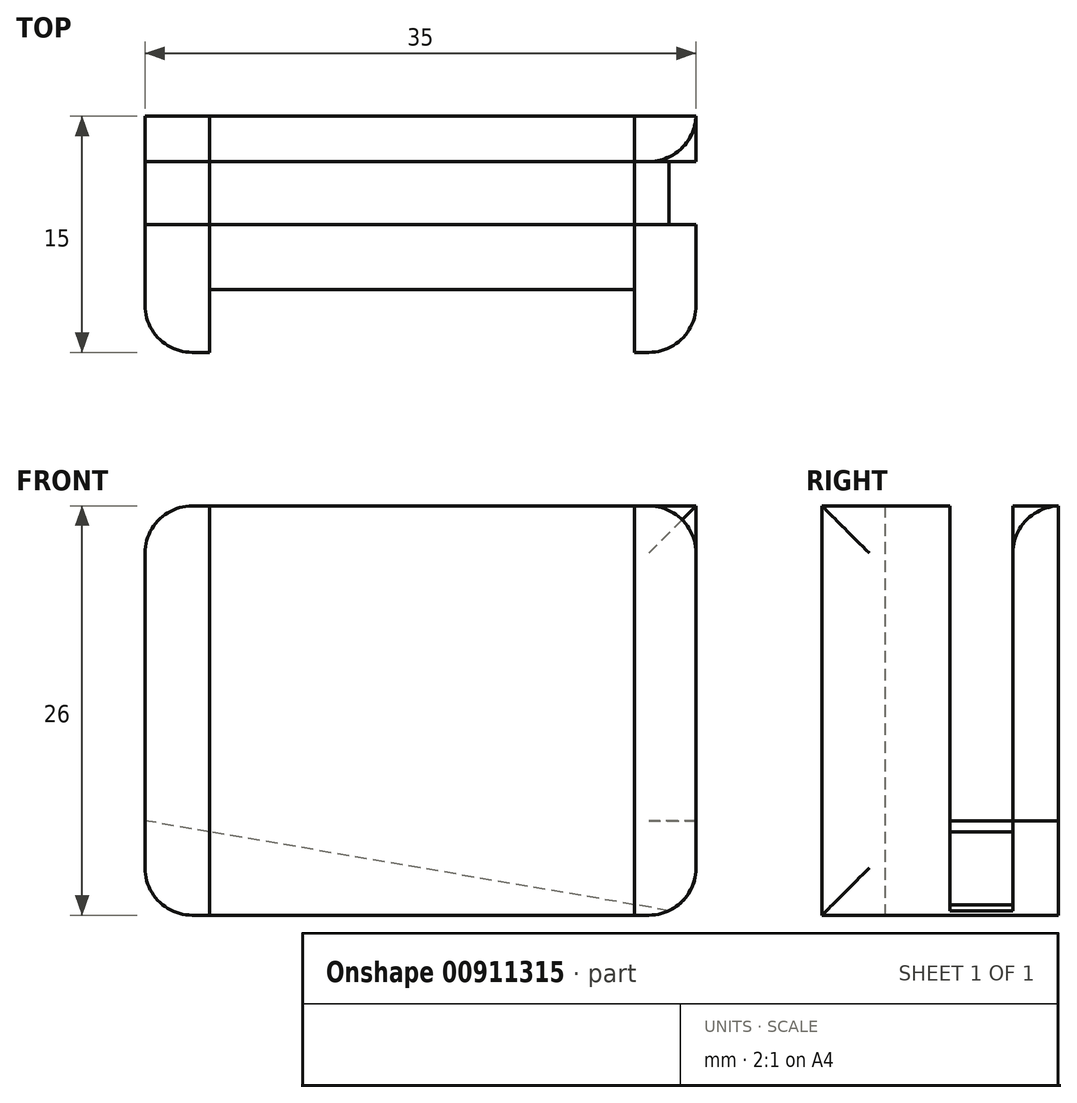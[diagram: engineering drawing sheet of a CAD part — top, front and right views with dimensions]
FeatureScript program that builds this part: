
annotation { "Feature Type Name" : "Feature", "Feature Type Description" : "" }
export const myFeature = defineFeature(function(context is Context, id is Id, definition is map)
    precondition{}
    {
        {
            var Q0;
            Q0=qCreatedBy(makeId("Front.planeOp"),FACE);
            var sketch = newSketch(context, id + "F0", { "sketchPlane" : qUnion([Q0])});
            skLineSegment(sketch, "E0.bottom", {"start": v(13, 13) * mm, "end": v(-14, 13) * mm});
            skLineSegment(sketch, "E0.top", {"start": v(14, -13) * mm, "end": v(-13, -13) * mm});
            skLineSegment(sketch, "E0.left", {"start": v(14, 13) * mm, "end": v(14, -13) * mm});
            skLineSegment(sketch, "E0.right", {"start": v(-13, 13) * mm, "end": v(-13, -13) * mm});
            skPoint(sketch, "E0.middle", {"position": v(0, 0) * mm});
            skLineSegment(sketch, "E1.bottom", {"start": v(17.91, 13) * mm, "end": v(-17.09, 13) * mm});
            skLineSegment(sketch, "E1.top", {"start": v(17.91, -13) * mm, "end": v(-17.09, -13) * mm});
            skLineSegment(sketch, "E1.left", {"start": v(17.91, 13) * mm, "end": v(17.91, -13) * mm});
            skLineSegment(sketch, "E1.right", {"start": v(-17.09, 13) * mm, "end": v(-17.09, -13) * mm});
            skSolve(sketch);
        }
        {
            var Q0;
            {var subQ0=sQuery(id+"F0.wireOp",EDGE,"E0.right");Q0=makeQuery(id+"F0.imprint","IMPRINT",FACE,{"disambiguationData":[TD([[makeQuery(id+"F0.imprint","IMPRINT",EDGE,{"derivedFrom":subQ0}),-1.0]])]});}
            var Q1;
            {var subQ0=sQuery(id+"F0.wireOp",EDGE,"E0.left");Q1=makeQuery(id+"F0.imprint","IMPRINT",FACE,{"disambiguationData":[TD([[makeQuery(id+"F0.imprint","IMPRINT",EDGE,{"derivedFrom":subQ0}),1.0]])]});}
            extrude(context, id + "F1", {"entities" : qUnion([Q0, Q1]), "depth" : 15 * mm, "offsetDistance" : 25 * mm});
        }
        {
            var Q0;
            {var subQ0=sQuery(id+"F0.wireOp",EDGE,"E0.left");Q0=makeQuery(id+"F0.imprint","IMPRINT",FACE,{"disambiguationData":[TD([[makeQuery(id+"F0.imprint","IMPRINT",EDGE,{"derivedFrom":subQ0}),-1.0]])]});}
            extrude(context, id + "F2", {"entities" : qUnion([Q0]), "depth" : 11 * mm, "offsetDistance" : 25 * mm});
        }
        {
            var Q0;
            Q0=makeQuery(id+"F2.opExtrude","SWEPT_FACE",FACE,{"disambiguationData":[OSD([sQuery(id+"F0.wireOp",EDGE,"E1.bottom")])]});
            var sketch = newSketch(context, id + "F3", { "sketchPlane" : qUnion([Q0])});
            skLineSegment(sketch, "E2.bottom", {"start": v(25.5, -2.88) * mm, "end": v(-24.5, -2.88) * mm});
            skLineSegment(sketch, "E2.top", {"start": v(25.5, -6.88) * mm, "end": v(-24.5, -6.88) * mm});
            skLineSegment(sketch, "E2.left", {"start": v(25.5, -2.88) * mm, "end": v(25.5, -6.88) * mm});
            skLineSegment(sketch, "E2.right", {"start": v(-24.5, -2.88) * mm, "end": v(-24.5, -6.88) * mm});
            skPoint(sketch, "E2.middle", {"position": v(0.5, -4.88) * mm});
            skPoint(sketch, "E2.middle.positionSnap0", {"position": v(0.5, -11) * mm});
            skPoint(sketch, "E2.centerSnap0", {"position": v(0.5, -11) * mm});
            skSolve(sketch);
        }
        {
            var Q0;
            Q0 = qSketchRegion(id + "F3", true);
            extrude(context, id + "F4", {"entities" : qUnion([Q0]), "operationType" : NewBodyOperationType.REMOVE, "oppositeDirection" : true, "depth" : 20 * mm, "offsetDistance" : 25 * mm});
        }
        {
            var Q0;
            Q0=makeQuery(id+"F1.opExtrude","SWEPT_EDGE",EDGE,{"disambiguationData":[OSD([sQuery(id+"F0.wireOp",EDGE,"E1.top"),sQuery(id+"F0.wireOp",EDGE,"E1.left")])]});
            cPoint(context, id + "F5", {"entities" : qUnion([Q0]), "parameter" : 0.5});
        }
        {
            var Q0;
            {var subQ0=sQuery(id+"F3.wireOp",EDGE,"E2.bottom");Q0=makeQuery(id+"F4.boolean.opBoolean","INTERSECT",VERTEX,{"derivedFrom":[makeQuery(id+"F1.opExtrude","SWEPT_FACE",FACE,{"disambiguationData":[OSD([sQuery(id+"F0.wireOp",EDGE,"E1.right")])]}),makeQuery(id+"F4.opExtrude","SWEPT_FACE",FACE,{"disambiguationData":[OSD([subQ0])]}),makeQuery(id+"F4.opExtrude","CAP_FACE",FACE,{"disambiguationData":[OSD([subQ0,sQuery(id+"F3.wireOp",EDGE,"E2.top"),sQuery(id+"F3.wireOp",EDGE,"E2.left"),sQuery(id+"F3.wireOp",EDGE,"E2.right")])],"isStart":false})]});}
            var Q1;
            {var subQ0=sQuery(id+"F3.wireOp",EDGE,"E2.top");Q1=makeQuery(id+"F4.boolean.opBoolean","INTERSECT",VERTEX,{"derivedFrom":[makeQuery(id+"F1.opExtrude","SWEPT_FACE",FACE,{"disambiguationData":[OSD([sQuery(id+"F0.wireOp",EDGE,"E1.right")])]}),makeQuery(id+"F4.opExtrude","CAP_FACE",FACE,{"disambiguationData":[OSD([sQuery(id+"F3.wireOp",EDGE,"E2.bottom"),subQ0,sQuery(id+"F3.wireOp",EDGE,"E2.left"),sQuery(id+"F3.wireOp",EDGE,"E2.right")])],"isStart":false}),makeQuery(id+"F4.opExtrude","SWEPT_FACE",FACE,{"disambiguationData":[OSD([subQ0])]})]});}
            var Q2;
            Q2 = qCreatedBy(id + "F5" ,VERTEX);
            cPlane(context, id + "F6", {"entities" : qUnion([Q0, Q1, Q2]), "cplaneType" : CPlaneType.THREE_POINT, "offset" : 25 * mm, "width" : 150 * mm, "height" : 150 * mm});
        }
        {
            var Q0;
            {var subQ0=sQuery(id+"F0.wireOp",EDGE,"E1.bottom");var subQ1=sQuery(id+"F3.wireOp",EDGE,"E2.top");Q0=makeQuery(id+"F4.boolean.opBoolean","COPY",EDGE,{"disambiguationData":[topologyDisambiguationEdgeConnected([makeQuery(id+"F1.opExtrude","SWEPT_FACE",FACE,{"disambiguationData":[OSD([subQ0]),TDD([makeQuery(id+"F0.imprint","IMPRINT",EDGE,{"disambiguationData":[TD([[makeQuery(id+"F0.imprint","INTERSECT",VERTEX,{"derivedFrom":[sQuery(id+"F0.wireOp",EDGE,"E0.right"),subQ0]}),-1.0]])],"derivedFrom":subQ0})])]})])],"derivedFrom":makeQuery(id+"F4.opExtrude","CAP_EDGE",EDGE,{"disambiguationData":[OSD([subQ1])],"isStart":true})});}
            var Q1;
            {var subQ0=sQuery(id+"F3.wireOp",EDGE,"E2.top");Q1=makeQuery(id+"F4.boolean.opBoolean","COPY",EDGE,{"disambiguationData":[topologyDisambiguationEdgeConnected([makeQuery(id+"F2.opExtrude","SWEPT_FACE",FACE,{"disambiguationData":[OSD([sQuery(id+"F0.wireOp",EDGE,"E1.bottom")])]})])],"derivedFrom":makeQuery(id+"F4.opExtrude","CAP_EDGE",EDGE,{"disambiguationData":[OSD([subQ0])],"isStart":true})});}
            var Q2;
            {var subQ0=sQuery(id+"F0.wireOp",EDGE,"E1.bottom");var subQ1=sQuery(id+"F3.wireOp",EDGE,"E2.top");Q2=makeQuery(id+"F4.boolean.opBoolean","COPY",EDGE,{"disambiguationData":[topologyDisambiguationEdgeConnected([makeQuery(id+"F1.opExtrude","SWEPT_FACE",FACE,{"disambiguationData":[OSD([subQ0]),TDD([makeQuery(id+"F0.imprint","IMPRINT",EDGE,{"disambiguationData":[TD([[makeQuery(id+"F0.imprint","INTERSECT",VERTEX,{"derivedFrom":[sQuery(id+"F0.wireOp",EDGE,"E0.left"),subQ0]}),1.0]])],"derivedFrom":subQ0})])]})])],"derivedFrom":makeQuery(id+"F4.opExtrude","CAP_EDGE",EDGE,{"disambiguationData":[OSD([subQ1])],"isStart":true})});}
            var Q3;
            {var subQ0=sQuery(id+"F0.wireOp",EDGE,"E1.left");var subQ1=sQuery(id+"F0.wireOp",EDGE,"E1.bottom");Q3=makeQuery(id+"F4.boolean.opBoolean","SPLIT",EDGE,{"disambiguationData":[TD([makeQuery(id+"F4.opExtrude","SWEPT_FACE",FACE,{"disambiguationData":[OSD([sQuery(id+"F3.wireOp",EDGE,"E2.top")])]})])],"derivedFrom":makeQuery(id+"F1.opExtrude","SWEPT_EDGE",EDGE,{"disambiguationData":[OSD([subQ1,subQ0])]})});}
            var Q4;
            {var subQ0=sQuery(id+"F0.wireOp",EDGE,"E1.right");var subQ1=sQuery(id+"F0.wireOp",EDGE,"E1.bottom");Q4=makeQuery(id+"F4.boolean.opBoolean","SPLIT",EDGE,{"disambiguationData":[TD([makeQuery(id+"F4.opExtrude","SWEPT_FACE",FACE,{"disambiguationData":[OSD([sQuery(id+"F3.wireOp",EDGE,"E2.top")])]})])],"derivedFrom":makeQuery(id+"F1.opExtrude","SWEPT_EDGE",EDGE,{"disambiguationData":[OSD([subQ1,subQ0])]})});}
            var Q5;
            Q5=makeQuery(id+"F1.opExtrude","CAP_EDGE",EDGE,{"disambiguationData":[OSD([sQuery(id+"F0.wireOp",EDGE,"E1.right")])],"isStart":false});
            var Q6;
            Q6=makeQuery(id+"F1.opExtrude","CAP_EDGE",EDGE,{"disambiguationData":[OSD([sQuery(id+"F0.wireOp",EDGE,"E1.left")])],"isStart":false});
            var Q7;
            {var subQ0=sQuery(id+"F3.wireOp",EDGE,"E2.bottom");Q7=makeQuery(id+"F4.boolean.opBoolean","COPY",EDGE,{"disambiguationData":[topologyDisambiguationEdgeConnected([makeQuery(id+"F2.opExtrude","SWEPT_FACE",FACE,{"disambiguationData":[OSD([sQuery(id+"F0.wireOp",EDGE,"E1.bottom")])]})])],"derivedFrom":makeQuery(id+"F4.opExtrude","CAP_EDGE",EDGE,{"disambiguationData":[OSD([subQ0])],"isStart":true})});}
            var Q8;
            {var subQ0=sQuery(id+"F0.wireOp",EDGE,"E1.bottom");var subQ1=sQuery(id+"F3.wireOp",EDGE,"E2.bottom");Q8=makeQuery(id+"F4.boolean.opBoolean","COPY",EDGE,{"disambiguationData":[topologyDisambiguationEdgeConnected([makeQuery(id+"F1.opExtrude","SWEPT_FACE",FACE,{"disambiguationData":[OSD([subQ0]),TDD([makeQuery(id+"F0.imprint","IMPRINT",EDGE,{"disambiguationData":[TD([[makeQuery(id+"F0.imprint","INTERSECT",VERTEX,{"derivedFrom":[sQuery(id+"F0.wireOp",EDGE,"E0.left"),subQ0]}),1.0]])],"derivedFrom":subQ0})])]})])],"derivedFrom":makeQuery(id+"F4.opExtrude","CAP_EDGE",EDGE,{"disambiguationData":[OSD([subQ1])],"isStart":true})});}
            var Q9;
            {var subQ0=sQuery(id+"F0.wireOp",EDGE,"E1.bottom");var subQ1=sQuery(id+"F3.wireOp",EDGE,"E2.bottom");Q9=makeQuery(id+"F4.boolean.opBoolean","COPY",EDGE,{"disambiguationData":[topologyDisambiguationEdgeConnected([makeQuery(id+"F1.opExtrude","SWEPT_FACE",FACE,{"disambiguationData":[OSD([subQ0]),TDD([makeQuery(id+"F0.imprint","IMPRINT",EDGE,{"disambiguationData":[TD([[makeQuery(id+"F0.imprint","INTERSECT",VERTEX,{"derivedFrom":[sQuery(id+"F0.wireOp",EDGE,"E0.right"),subQ0]}),-1.0]])],"derivedFrom":subQ0})])]})])],"derivedFrom":makeQuery(id+"F4.opExtrude","CAP_EDGE",EDGE,{"disambiguationData":[OSD([subQ1])],"isStart":true})});}
            var Q10;
            {var subQ0=sQuery(id+"F0.wireOp",EDGE,"E1.right");var subQ1=sQuery(id+"F0.wireOp",EDGE,"E1.bottom");Q10=makeQuery(id+"F4.boolean.opBoolean","SPLIT",EDGE,{"disambiguationData":[TD([makeQuery(id+"F4.opExtrude","SWEPT_FACE",FACE,{"disambiguationData":[OSD([sQuery(id+"F3.wireOp",EDGE,"E2.bottom")])]})])],"derivedFrom":makeQuery(id+"F1.opExtrude","SWEPT_EDGE",EDGE,{"disambiguationData":[OSD([subQ1,subQ0])]})});}
            var Q11;
            Q11=makeQuery(id+"F4.boolean.opBoolean","INTERSECT",EDGE,{"derivedFrom":[makeQuery(id+"F1.opExtrude","SWEPT_FACE",FACE,{"disambiguationData":[OSD([sQuery(id+"F0.wireOp",EDGE,"E1.left")])]}),makeQuery(id+"F4.opExtrude","SWEPT_FACE",FACE,{"disambiguationData":[OSD([sQuery(id+"F3.wireOp",EDGE,"E2.bottom")])]})]});
            var Q12;
            Q12=makeQuery(id+"F1.opExtrude","SWEPT_EDGE",EDGE,{"disambiguationData":[OSD([sQuery(id+"F0.wireOp",EDGE,"E1.top"),sQuery(id+"F0.wireOp",EDGE,"E1.left")])]});
            var Q13;
            Q13=makeQuery(id+"F1.opExtrude","SWEPT_EDGE",EDGE,{"disambiguationData":[OSD([sQuery(id+"F0.wireOp",EDGE,"E1.top"),sQuery(id+"F0.wireOp",EDGE,"E1.right")])]});
            fillet(context, id + "F7", {"entities" : qUnion([Q0, Q1, Q2, Q3, Q4, Q5, Q6, Q7, Q8, Q9, Q10, Q11, Q12, Q13]), "radius" : 3 * mm, "tangentPropagation" : true, "allowEdgeOverflow" : false});
        }
        {
            var Q0;
            Q0 = qSketchRegion(id + "F3", true);
            var Q1;
            Q1=qCreatedBy(id+"F6.planeOp",FACE);
            extrude(context, id + "F8", {"entities" : qUnion([Q0]), "operationType" : NewBodyOperationType.REMOVE, "endBound" : BoundingType.UP_TO_SURFACE, "oppositeDirection" : true, "depth" : 25 * mm, "endBoundEntityFace" : qUnion([Q1]), "offsetDistance" : 25 * mm});
        }
    });
